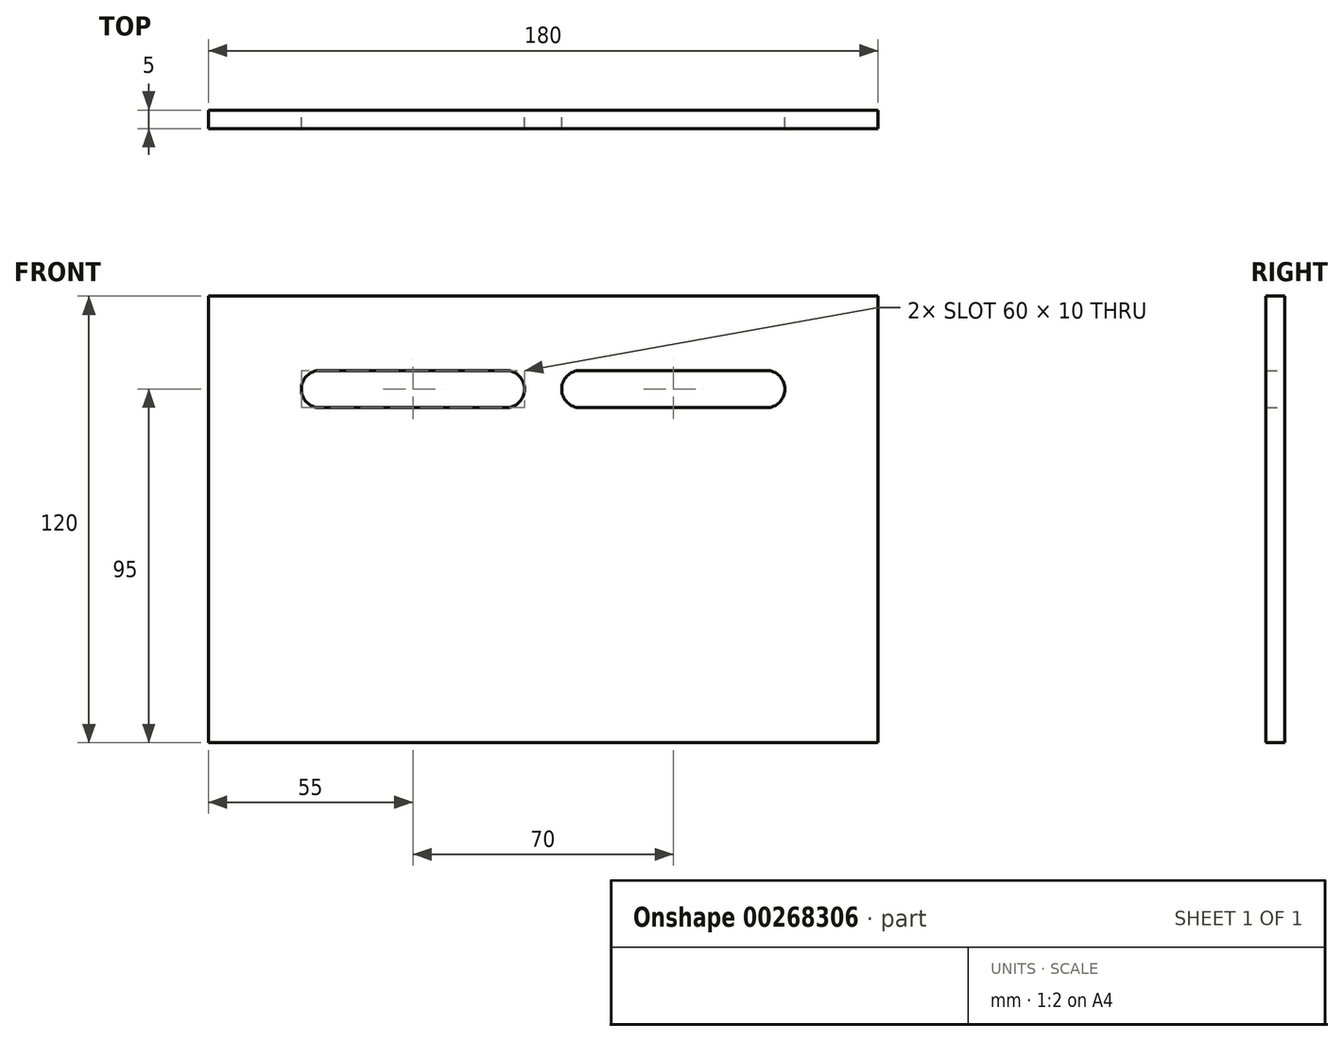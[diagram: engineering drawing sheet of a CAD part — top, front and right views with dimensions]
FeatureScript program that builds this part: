
annotation { "Feature Type Name" : "Feature", "Feature Type Description" : "" }
export const myFeature = defineFeature(function(context is Context, id is Id, definition is map)
    precondition{}
    {
        {
            var Q0;
            Q0=qCreatedBy(makeId("Front.planeOp"),FACE);
            var sketch = newSketch(context, id + "F0", { "sketchPlane" : qUnion([Q0])});
            skLineSegment(sketch, "E0.bottom", {"start": v(0, 0) * mm, "end": v(180, 0) * mm});
            skLineSegment(sketch, "E0.top", {"start": v(0, 120) * mm, "end": v(180, 120) * mm});
            skLineSegment(sketch, "E0.left", {"start": v(0, 0) * mm, "end": v(0, 120) * mm});
            skLineSegment(sketch, "E0.right", {"start": v(180, 0) * mm, "end": v(180, 120) * mm});
            skLineSegment(sketch, "E1.bottom", {"start": v(30, 100) * mm, "end": v(80, 100) * mm});
            skLineSegment(sketch, "E1.top", {"start": v(30, 90) * mm, "end": v(80, 90) * mm});
            skLineSegment(sketch, "E1.left", {"start": v(30, 100) * mm, "end": v(30, 90) * mm});
            skLineSegment(sketch, "E1.right", {"start": v(80, 100) * mm, "end": v(80, 90) * mm});
            skLineSegment(sketch, "E2.bottom", {"start": v(100, 100) * mm, "end": v(150, 100) * mm});
            skLineSegment(sketch, "E2.top", {"start": v(100, 90) * mm, "end": v(150, 90) * mm});
            skLineSegment(sketch, "E2.left", {"start": v(100, 100) * mm, "end": v(100, 90) * mm});
            skLineSegment(sketch, "E2.right", {"start": v(150, 100) * mm, "end": v(150, 90) * mm});
            skArc(sketch, "E3", {"start": v(30, 100) * mm, "mid": v(25, 95) * mm, "end": v(30, 90) * mm});
            skArc(sketch, "E4", {"start": v(100, 100) * mm, "mid": v(95, 95) * mm, "end": v(100, 90) * mm});
            skArc(sketch, "E5", {"start": v(80, 90) * mm, "mid": v(85, 95) * mm, "end": v(80, 100) * mm});
            skArc(sketch, "E6", {"start": v(150, 90) * mm, "mid": v(155, 95) * mm, "end": v(150, 100) * mm});
            skSolve(sketch);
        }
        {
            var Q0;
            Q0=makeQuery(id+"F0.imprint","IMPRINT",FACE,{"disambiguationData":[TD([[makeQuery(id+"F0.imprint","IMPRINT",EDGE,{"derivedFrom":sQuery(id+"F0.wireOp",EDGE,"E0.bottom")}),1.0]])]});
            extrude(context, id + "F1", {"entities" : qUnion([Q0]), "offsetDistance" : 25 * mm, "depth" : 5 * mm});
        }
    });
